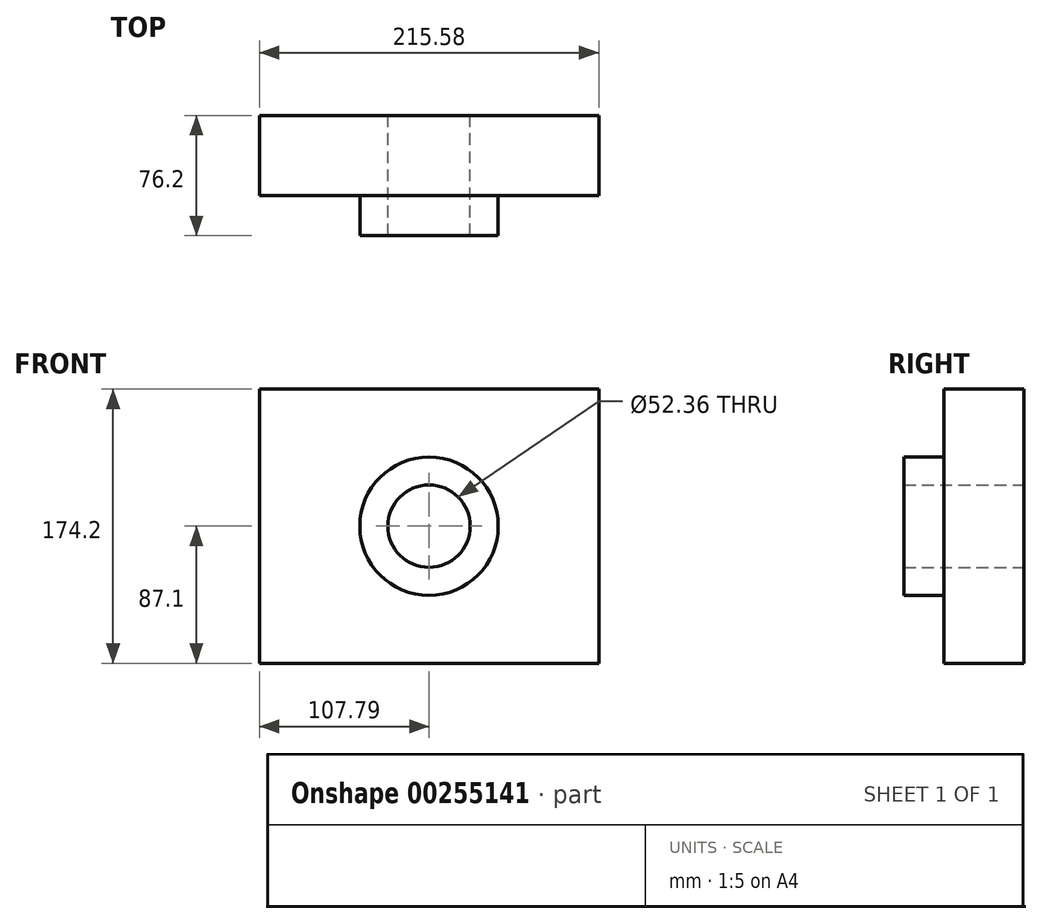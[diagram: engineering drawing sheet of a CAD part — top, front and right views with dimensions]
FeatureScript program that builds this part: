
annotation { "Feature Type Name" : "Feature", "Feature Type Description" : "" }
export const myFeature = defineFeature(function(context is Context, id is Id, definition is map)
    precondition{}
    {
        {
            var Q0;
            Q0=qCreatedBy(makeId("Front.planeOp"),FACE);
            var sketch = newSketch(context, id + "F0", { "sketchPlane" : qUnion([Q0])});
            skLineSegment(sketch, "E0.bottom", {"start": v(-107.79, 87.1) * mm, "end": v(107.79, 87.1) * mm});
            skLineSegment(sketch, "E0.top", {"start": v(-107.79, -87.1) * mm, "end": v(107.79, -87.1) * mm});
            skLineSegment(sketch, "E0.left", {"start": v(-107.79, 87.1) * mm, "end": v(-107.79, -87.1) * mm});
            skLineSegment(sketch, "E0.right", {"start": v(107.79, 87.1) * mm, "end": v(107.79, -87.1) * mm});
            skPoint(sketch, "E0.middle", {"position": v(0, 0) * mm});
            skCircle(sketch, "E1", {"center": v(0, 0) * mm, "radius": 26.18 * mm});
            skSolve(sketch);
        }
        {
            var Q0;
            Q0 = qSketchRegion(id + "F0", true);
            extrude(context, id + "F1", {"entities" : qUnion([Q0]), "depth" : 50.8 * mm});
        }
        {
            var Q0;
            Q0=makeQuery(id+"F1.opExtrude","CAP_FACE",FACE,{"disambiguationData":[OSD([sQuery(id+"F0.wireOp",EDGE,"E0.bottom"),sQuery(id+"F0.wireOp",EDGE,"E0.top"),sQuery(id+"F0.wireOp",EDGE,"E0.left"),sQuery(id+"F0.wireOp",EDGE,"E0.right"),sQuery(id+"F0.wireOp",EDGE,"E1")])],"isStart":false});
            var sketch = newSketch(context, id + "F2", { "sketchPlane" : qUnion([Q0])});
            skCircle(sketch, "E2.0", {"center": v(0, 0) * mm, "radius": 43.96 * mm});
            skSolve(sketch);
        }
        {
            var Q0;
            Q0=makeQuery(id+"F2.imprint","IMPRINT",FACE,{"disambiguationData":[TD([[makeQuery(id+"F2.imprint","IMPRINT",EDGE,{"derivedFrom":sQuery(id+"F2.wireOp",EDGE,"E2.0")}),1.0]])]});
            extrude(context, id + "F3", {"entities" : qUnion([Q0]), "operationType" : NewBodyOperationType.ADD, "depth" : 25.4 * mm});
        }
    });
